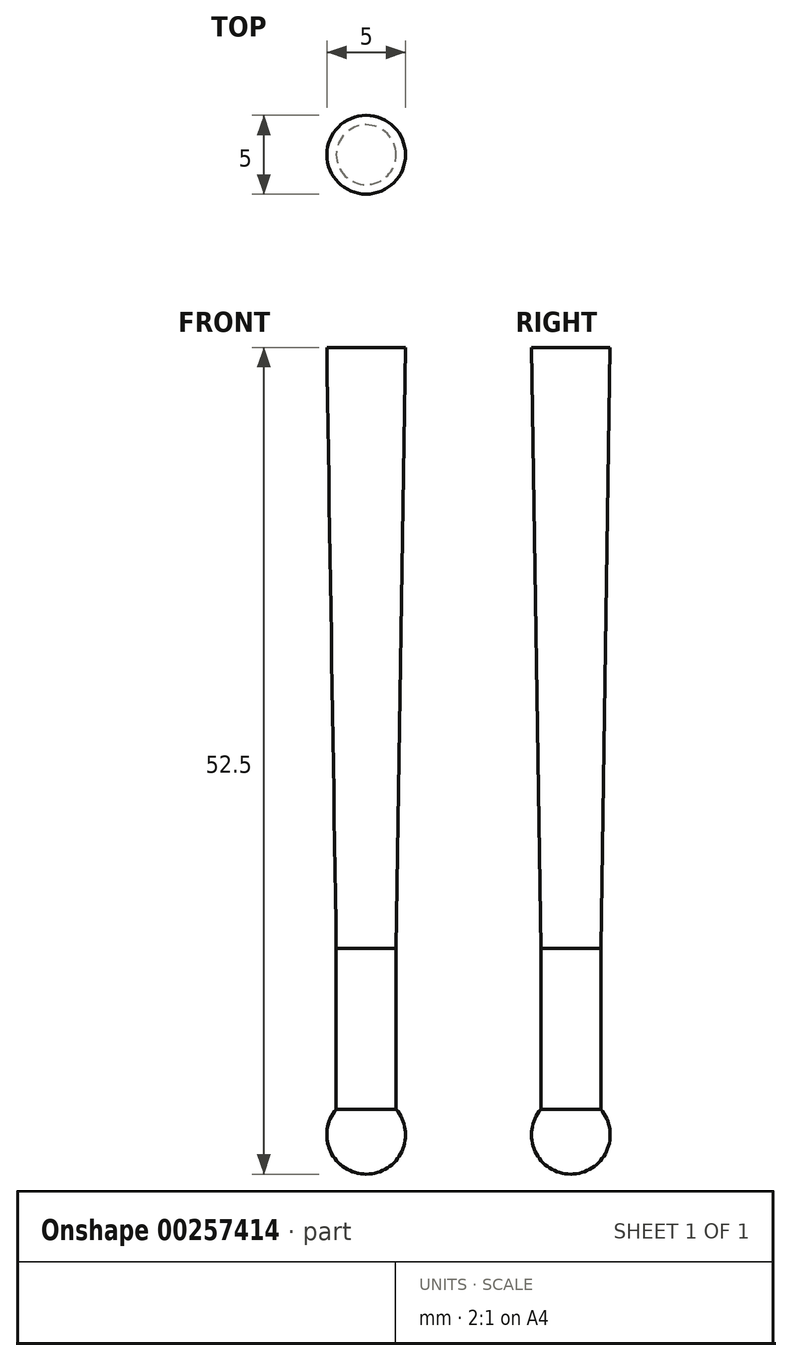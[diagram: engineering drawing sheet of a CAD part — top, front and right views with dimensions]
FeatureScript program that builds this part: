
annotation { "Feature Type Name" : "Feature", "Feature Type Description" : "" }
export const myFeature = defineFeature(function(context is Context, id is Id, definition is map)
    precondition{}
    {
        {
            var Q0;
            Q0=qCreatedBy(makeId("Front.planeOp"),FACE);
            var sketch = newSketch(context, id + "F0", { "sketchPlane" : qUnion([Q0])});
            skLineSegment(sketch, "E0", {"start": v(0, 0) * mm, "end": v(0, 50) * mm});
            skLineSegment(sketch, "E1", {"start": v(0, 50) * mm, "end": v(2.5, 50) * mm});
            skArc(sketch, "E2", {"start": v(0, -2.5) * mm, "mid": v(2.27, -1.05) * mm, "end": v(1.9, 1.62) * mm});
            skLineSegment(sketch, "E3", {"start": v(1.9, 11.84) * mm, "end": v(1.9, 1.62) * mm});
            skFitSpline(sketch, "E4", {"points": [v(2.5, 50) * mm, v(1.9, 11.84) * mm], "startDerivative": vector(-0.6, -38.16) * mm, "endDerivative": vector(-0.6, -38.16) * mm});
            skLineSegment(sketch, "E5", {"start": v(0, 0) * mm, "end": v(0, -2.5) * mm});
            skSolve(sketch);
        }
        {
            var Q0;
            Q0 = qSketchRegion(id + "F0", true);
            var Q1;
            Q1=sQuery(id+"F0.wireOp",EDGE,"E0");
            revolve(context, id + "F1", {"entities" : qUnion([Q0]), "axis" : qUnion([Q1]), "revolveType" : RevolveType.FULL});
        }
    });
